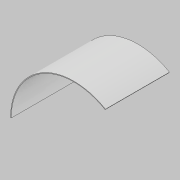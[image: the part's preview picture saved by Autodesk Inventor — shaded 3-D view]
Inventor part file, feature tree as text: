
AUTODESK INVENTOR PART (.ipt)
format: ipt  version: 2021 (Build 250183000, 183)  size: 96,768 bytes
history: native  units: mm
features: extrude x1, sketch x1
ambient origin geometry x8: Origin, YZ Plane, XZ Plane, XY Plane, X Axis, Y Axis, Z Axis, Center Point
bodies: Solid1 (feature_tree)
feature tree (2):
  extrude  "Extrusion1"  Depth=890.0mm
  sketch  "Sketch1"  dims[d0=10.0mm d1=890.0mm d2=0.0mm d4=900.0mm d5=0.0mm d6=120.0deg]
